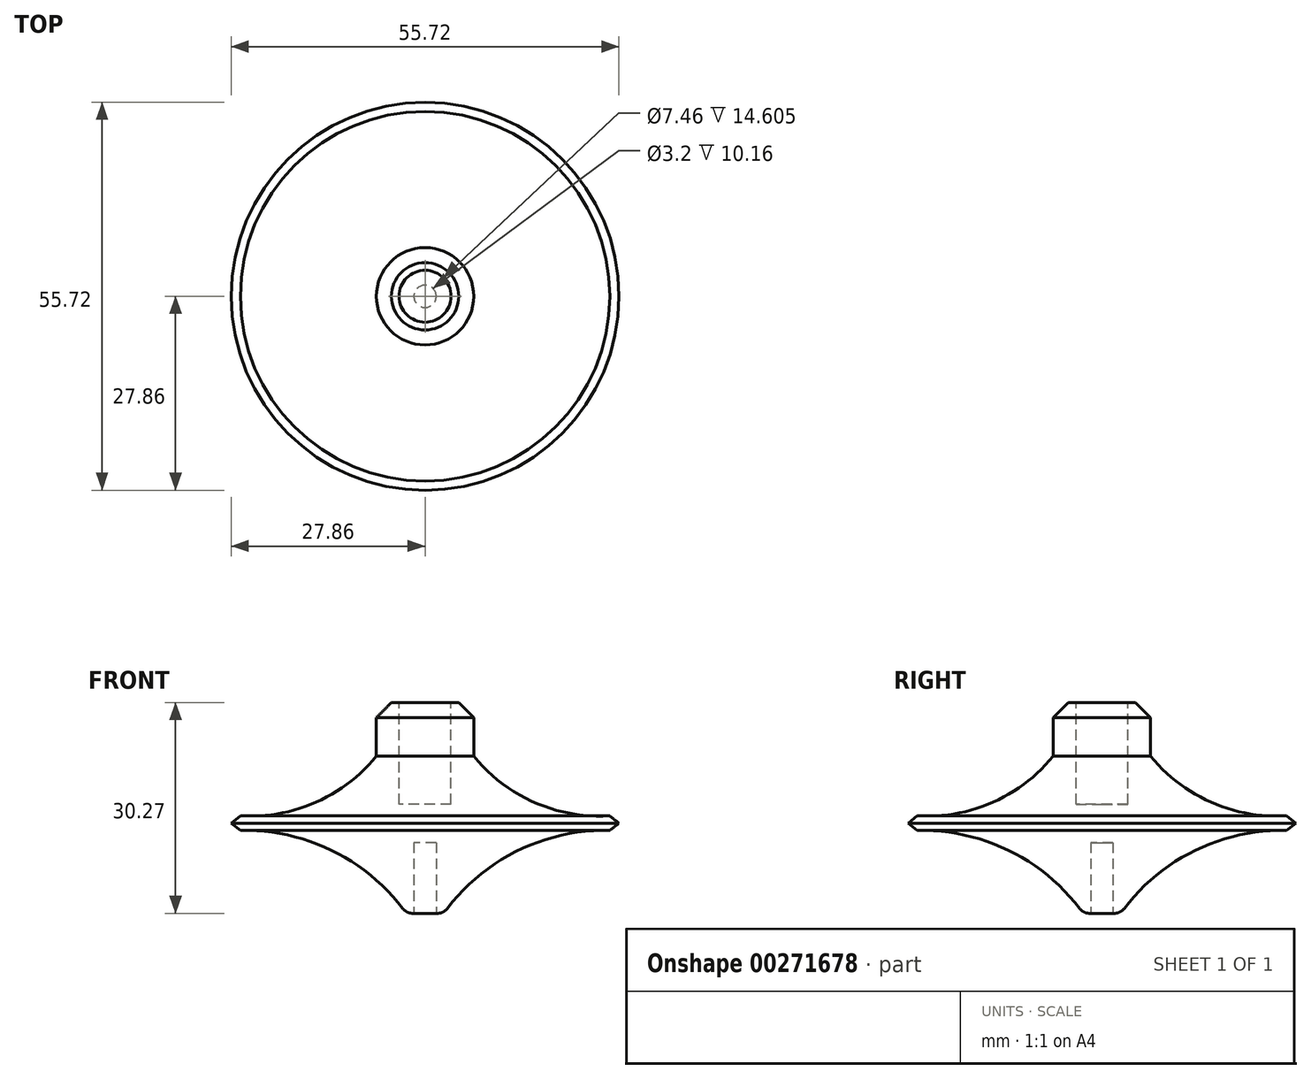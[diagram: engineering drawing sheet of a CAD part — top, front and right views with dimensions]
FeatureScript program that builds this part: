
annotation { "Feature Type Name" : "Feature", "Feature Type Description" : "" }
export const myFeature = defineFeature(function(context is Context, id is Id, definition is map)
    precondition{}
    {
        {
            var Q0;
            Q0=qCreatedBy(makeId("Right.planeOp"),FACE);
            var sketch = newSketch(context, id + "F0", { "sketchPlane" : qUnion([Q0])});
            skLineSegment(sketch, "E0", {"start": v(0, 0) * mm, "end": v(2.69, 0) * mm});
            skArc(sketch, "E1", {"start": v(26.54, 11.9) * mm, "mid": v(13.14, 8.9) * mm, "end": v(2.69, 0) * mm});
            skLineSegment(sketch, "E2", {"start": v(26.54, 11.9) * mm, "end": v(27.86, 12.95) * mm});
            skLineSegment(sketch, "E3", {"start": v(27.86, 12.95) * mm, "end": v(26.54, 13.99) * mm});
            skArc(sketch, "E4", {"start": v(7, 22.57) * mm, "mid": v(15.74, 15.93) * mm, "end": v(26.54, 13.99) * mm});
            skLineSegment(sketch, "E5", {"start": v(7, 22.57) * mm, "end": v(7, 30.27) * mm});
            skLineSegment(sketch, "E6", {"start": v(7, 30.27) * mm, "end": v(0, 30.27) * mm});
            skLineSegment(sketch, "E7", {"start": v(0, 30.27) * mm, "end": v(0, 0) * mm});
            skSolve(sketch);
        }
        {
            var Q0;
            Q0=makeQuery(id+"F0.imprint","IMPRINT",FACE,{"disambiguationData":[TD([[makeQuery(id+"F0.imprint","IMPRINT",EDGE,{"derivedFrom":sQuery(id+"F0.wireOp",EDGE,"E0")}),1.0]])]});
            var Q1;
            Q1=sQuery(id+"F0.wireOp",EDGE,"E7");
            revolve(context, id + "F1", {"entities" : qUnion([Q0]), "axis" : qUnion([Q1]), "revolveType" : RevolveType.FULL});
        }
        {
            var Q0;
            Q0=makeQuery(id+"F1.opRevolve","SWEPT_FACE",FACE,{"disambiguationData":[OSD([sQuery(id+"F0.wireOp",EDGE,"E6")])]});
            var sketch = newSketch(context, id + "F2", { "sketchPlane" : qUnion([Q0])});
            skCircle(sketch, "E8", {"center": v(0, 0) * mm, "radius": 4.76 * mm});
            skSolve(sketch);
        }
        {
            var Q0;
            Q0=makeQuery(id+"F2.imprint","IMPRINT",FACE,{"disambiguationData":[TD([[makeQuery(id+"F2.imprint","IMPRINT",EDGE,{"derivedFrom":sQuery(id+"F2.wireOp",EDGE,"E8")}),1.0]])]});
            extrude(context, id + "F3", {"entities" : qUnion([Q0]), "operationType" : NewBodyOperationType.ADD, "oppositeDirection" : true, "depth" : 14.6 * mm});
        }
        {
            var Q0;
            Q0=qCreatedBy(makeId("Top.planeOp"),FACE);
            var sketch = newSketch(context, id + "F4", { "sketchPlane" : qUnion([Q0])});
            skCircle(sketch, "E9", {"center": v(0, 0) * mm, "radius": 1.6 * mm});
            skSolve(sketch);
        }
        {
            var Q0;
            Q0=makeQuery(id+"F4.imprint","IMPRINT",FACE,{"disambiguationData":[TD([[makeQuery(id+"F4.imprint","IMPRINT",EDGE,{"derivedFrom":sQuery(id+"F4.wireOp",EDGE,"E9")}),1.0]])]});
            extrude(context, id + "F5", {"entities" : qUnion([Q0]), "operationType" : NewBodyOperationType.ADD, "depth" : 10.16 * mm});
        }
        {
            var Q0;
            Q0=makeQuery(id+"F1.opRevolve","SWEPT_FACE",FACE,{"disambiguationData":[OSD([sQuery(id+"F0.wireOp",EDGE,"E6")])]});
            var sketch = newSketch(context, id + "F6", { "sketchPlane" : qUnion([Q0])});
            skCircle(sketch, "E10", {"center": v(0, 0) * mm, "radius": 4.78 * mm});
            skSolve(sketch);
        }
        {
            var Q0;
            Q0=makeQuery(id+"F6.imprint","IMPRINT",FACE,{"disambiguationData":[TD([[makeQuery(id+"F6.imprint","IMPRINT",EDGE,{"derivedFrom":sQuery(id+"F6.wireOp",EDGE,"E10")}),1.0]])]});
            extrude(context, id + "F7", {"entities" : qUnion([Q0]), "operationType" : NewBodyOperationType.ADD, "oppositeDirection" : true, "depth" : 14.6 * mm});
        }
        {
            var Q0;
            Q0=makeQuery(id+"F1.opRevolve","SWEPT_FACE",FACE,{"disambiguationData":[OSD([sQuery(id+"F0.wireOp",EDGE,"E6")])]});
            var sketch = newSketch(context, id + "F8", { "sketchPlane" : qUnion([Q0])});
            skCircle(sketch, "E11", {"center": v(0, 0) * mm, "radius": 3.73 * mm});
            skSolve(sketch);
        }
        {
            var Q0;
            Q0=makeQuery(id+"F8.imprint","IMPRINT",FACE,{"disambiguationData":[TD([[makeQuery(id+"F8.imprint","IMPRINT",EDGE,{"derivedFrom":sQuery(id+"F8.wireOp",EDGE,"E11")}),1.0]])]});
            extrude(context, id + "F9", {"entities" : qUnion([Q0]), "operationType" : NewBodyOperationType.REMOVE, "oppositeDirection" : true, "depth" : 14.6 * mm});
        }
        {
            var Q0;
            Q0=qCreatedBy(makeId("Top.planeOp"),FACE);
            var sketch = newSketch(context, id + "F10", { "sketchPlane" : qUnion([Q0])});
            skCircle(sketch, "E12", {"center": v(0, 0) * mm, "radius": 1.6 * mm});
            skSolve(sketch);
        }
        {
            var Q0;
            Q0=makeQuery(id+"F10.imprint","IMPRINT",FACE,{"disambiguationData":[TD([[makeQuery(id+"F10.imprint","IMPRINT",EDGE,{"derivedFrom":sQuery(id+"F10.wireOp",EDGE,"E12")}),1.0]])]});
            extrude(context, id + "F11", {"entities" : qUnion([Q0]), "operationType" : NewBodyOperationType.REMOVE, "depth" : 10.16 * mm});
        }
        {
            var Q0;
            Q0=makeQuery(id+"F1.opRevolve","SWEPT_EDGE",EDGE,{"disambiguationData":[OSD([sQuery(id+"F0.wireOp",EDGE,"E5"),sQuery(id+"F0.wireOp",EDGE,"E6")])]});
            chamfer(context, id + "F12", {"entities" : qUnion([Q0]), "width" : 2.16 * mm, "tangentPropagation" : true});
        }
        {
            var Q0;
            Q0=makeQuery(id+"F1.opRevolve","SWEPT_EDGE",EDGE,{"disambiguationData":[OSD([sQuery(id+"F0.wireOp",EDGE,"E0"),sQuery(id+"F0.wireOp",EDGE,"E1")])]});
            fillet(context, id + "F13", {"entities" : qUnion([Q0]), "radius" : 1.78 * mm, "tangentPropagation" : true, "allowEdgeOverflow" : false});
        }
    });
